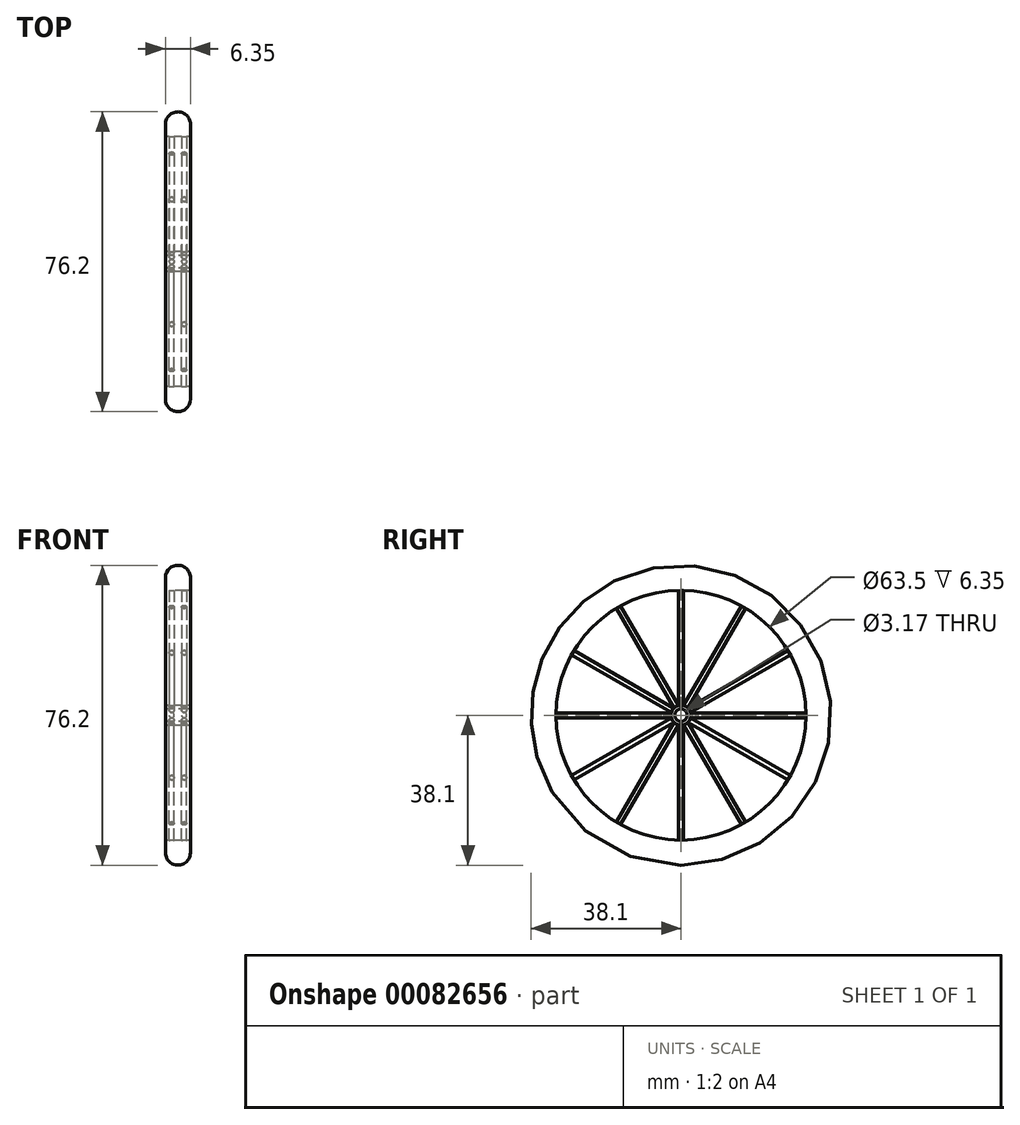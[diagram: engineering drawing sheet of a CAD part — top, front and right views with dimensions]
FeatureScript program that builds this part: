
annotation { "Feature Type Name" : "Feature", "Feature Type Description" : "" }
export const myFeature = defineFeature(function(context is Context, id is Id, definition is map)
    precondition{}
    {
        {
            var Q0;
            Q0=qCreatedBy(makeId("Right.planeOp"),FACE);
            var sketch = newSketch(context, id + "F0", { "sketchPlane" : qUnion([Q0])});
            skCircle(sketch, "E0", {"center": v(0, 0) * mm, "radius": 38.1 * mm});
            skCircle(sketch, "E1", {"center": v(0, 0) * mm, "radius": 31.75 * mm});
            skSolve(sketch);
        }
        {
            var Q0;
            Q0 = qSketchRegion(id + "F0", true);
            extrude(context, id + "F1", {"entities" : qUnion([Q0]), "depth" : 6.35 * mm});
        }
        {
            var Q0;
            Q0=makeQuery(id+"F1.opExtrude","CAP_EDGE",EDGE,{"disambiguationData":[OSD([sQuery(id+"F0.wireOp",EDGE,"E0")])],"isStart":false});
            var Q1;
            Q1=makeQuery(id+"F1.opExtrude","CAP_EDGE",EDGE,{"disambiguationData":[OSD([sQuery(id+"F0.wireOp",EDGE,"E0")])],"isStart":true});
            fillet(context, id + "F2", {"entities" : qUnion([Q0, Q1]), "radius" : 3.17 * mm, "tangentPropagation" : true, "allowEdgeOverflow" : false});
        }
        {
            var Q0;
            Q0=qCreatedBy(makeId("Top.planeOp"),FACE);
            var sketch = newSketch(context, id + "F3", { "sketchPlane" : qUnion([Q0])});
            skLineSegment(sketch, "E2", {"start": v(0, 0) * mm, "end": v(3.18, 0) * mm});
            skLineSegment(sketch, "E3", {"start": v(3.18, 0) * mm, "end": v(6.35, 0) * mm});
            skCircle(sketch, "E4", {"center": v(4.76, 0) * mm, "radius": 0.64 * mm});
            skCircle(sketch, "E5", {"center": v(1.59, 0) * mm, "radius": 0.64 * mm});
            skSolve(sketch);
        }
        {
            var Q0;
            Q0 = qSketchRegion(id + "F3", true);
            extrude(context, id + "F4", {"entities" : qUnion([Q0]), "depth" : 33.02 * mm});
        }
        {
            var Q0;
            Q0=makeQuery(id+"F4.opExtrude","SWEPT_BODY",BODY,{"disambiguationData":[OSD([sQuery(id+"F3.wireOp",EDGE,"E4")])]});
            var Q1;
            Q1=makeQuery(id+"F4.opExtrude","SWEPT_BODY",BODY,{"disambiguationData":[OSD([sQuery(id+"F3.wireOp",EDGE,"E5")])]});
            var Q2;
            {var subQ0=sQuery(id+"F0.wireOp",EDGE,"E0");Q2=makeQuery(id+"F2.opFillet","BLEND_EDGE",EDGE,{"blendedFrom":[makeQuery(id+"F1.opExtrude","CAP_EDGE",EDGE,{"disambiguationData":[OSD([subQ0])],"isStart":false}),makeQuery(id+"F1.opExtrude","CAP_FACE",FACE,{"disambiguationData":[OSD([subQ0,sQuery(id+"F0.wireOp",EDGE,"E1")])],"isStart":false})],"blendedInto":[makeQuery(id+"F1.opExtrude","CAP_FACE",FACE,{"disambiguationData":[OSD([subQ0,sQuery(id+"F0.wireOp",EDGE,"E1")])],"isStart":false})]});}
            circularPattern(context, id + "F5", {"operationType" : NewBodyOperationType.ADD, "entities" : qUnion([Q0, Q1]), "axis" : qUnion([Q2]), "angle" : 30 * degree, "instanceCount" : 12});
        }
        {
            var Q0;
            Q0=qCreatedBy(makeId("Right.planeOp"),FACE);
            var sketch = newSketch(context, id + "F6", { "sketchPlane" : qUnion([Q0])});
            skCircle(sketch, "E6", {"center": v(0, 0) * mm, "radius": 1.59 * mm});
            skSolve(sketch);
        }
        {
            var Q0;
            Q0 = qSketchRegion(id + "F6", true);
            extrude(context, id + "F7", {"entities" : qUnion([Q0]), "operationType" : NewBodyOperationType.REMOVE, "depth" : 25.4 * mm});
        }
        {
            var Q0;
            Q0=qCreatedBy(makeId("Right.planeOp"),FACE);
            var sketch = newSketch(context, id + "F8", { "sketchPlane" : qUnion([Q0])});
            skCircle(sketch, "E7", {"center": v(0, 0) * mm, "radius": 1.59 * mm});
            skCircle(sketch, "E8", {"center": v(0, 0) * mm, "radius": 2.54 * mm});
            skSolve(sketch);
        }
        {
            var Q0;
            Q0 = qSketchRegion(id + "F8", true);
            extrude(context, id + "F9", {"entities" : qUnion([Q0]), "operationType" : NewBodyOperationType.ADD, "depth" : 6.35 * mm});
        }
    });
